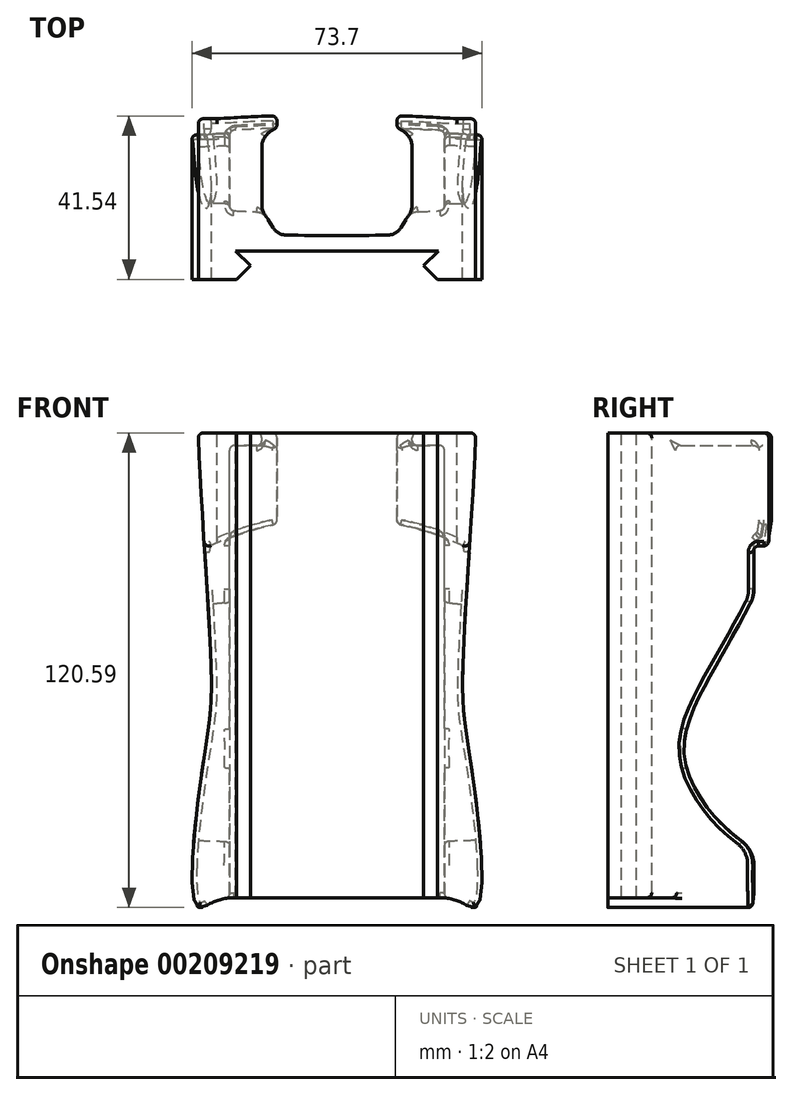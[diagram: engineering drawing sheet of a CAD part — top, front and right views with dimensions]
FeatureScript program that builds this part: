
annotation { "Feature Type Name" : "Feature", "Feature Type Description" : "" }
export const myFeature = defineFeature(function(context is Context, id is Id, definition is map)
    precondition{}
    {
        {
            var Q0;
            Q0=qCreatedBy(makeId("Top.planeOp"),FACE);
            var sketch = newSketch(context, id + "F0", { "sketchPlane" : qUnion([Q0])});
            skLineSegment(sketch, "E0", {"start": v(30.48, -10.36) * mm, "end": v(30.48, 30.47) * mm});
            skLineSegment(sketch, "E1", {"start": v(27.3, 27.49) * mm, "end": v(27.3, 7.17) * mm});
            skArc(sketch, "E2", {"start": v(20.63, 6.82) * mm, "mid": v(23.97, 6.98) * mm, "end": v(27.3, 7.17) * mm});
            skArc(sketch, "E3", {"start": v(0, 0.76) * mm, "mid": v(6.56, 0.8) * mm, "end": v(13.12, 0.95) * mm});
            skLineSegment(sketch, "E4", {"start": v(16.3, 2.85) * mm, "end": v(17.5, 4.91) * mm});
            skPoint(sketch, "E5.orphan", {"position": v(15.25, 1.01) * mm});
            skPoint(sketch, "E6.visualSharp", {"position": v(18.55, 6.73) * mm});
            skArc(sketch, "E6.filletArc", {"start": v(20.63, 6.82) * mm, "mid": v(18.82, 6.27) * mm, "end": v(17.5, 4.91) * mm});
            skArc(sketch, "E7.filletArc", {"start": v(13.12, 0.95) * mm, "mid": v(14.96, 1.48) * mm, "end": v(16.3, 2.85) * mm});
            skLineSegment(sketch, "E8", {"start": v(0, 0) * mm, "end": v(0, -3.13) * mm});
            skArc(sketch, "E9", {"start": v(27.3, 27.49) * mm, "mid": v(21.28, 27.8) * mm, "end": v(15.25, 28.05) * mm});
            skArc(sketch, "E10", {"start": v(30.48, 30.47) * mm, "mid": v(22.87, 30.9) * mm, "end": v(15.25, 31.22) * mm});
            skPoint(sketch, "E11.start.orphan", {"position": v(30.48, 27.99) * mm});
            skLineSegment(sketch, "E12.trimOffspring", {"start": v(0, 0.76) * mm, "end": v(0, -3.13) * mm});
            skLineSegment(sketch, "E13", {"start": v(15.25, 31.22) * mm, "end": v(15.25, 28.05) * mm});
            skLineSegment(sketch, "E14", {"start": v(0, -3.13) * mm, "end": v(25.78, -3.13) * mm});
            skLineSegment(sketch, "E15", {"start": v(25.78, -3.13) * mm, "end": v(22.02, -6.89) * mm});
            skLineSegment(sketch, "E16", {"start": v(0, -6.89) * mm, "end": v(29.89, -6.89) * mm, "construction": true});
            skLineSegment(sketch, "E17", {"start": v(25.5, -10.36) * mm, "end": v(30.48, -10.36) * mm});
            skLineSegment(sketch, "E18", {"start": v(22.02, -6.89) * mm, "end": v(25.5, -10.36) * mm});
            skSolve(sketch);
        }
        {
            var Q0;
            Q0=qSketchRegion(id+"F0",true);
            extrude(context, id + "F1", {"entities" : qUnion([Q0]), "oppositeDirection" : true, "depth" : 118.11 * mm});
        }
        {
            var Q0;
            Q0=makeQuery(id+"F1.opExtrude","SWEPT_FACE",FACE,{"disambiguationData":[OSD([sQuery(id+"F0.wireOp",EDGE,"E17")])]});
            var sketch = newSketch(context, id + "F2", { "sketchPlane" : qUnion([Q0])});
            skLineSegment(sketch, "E19", {"start": v(30.48, 0) * mm, "end": v(35.28, 0) * mm});
            skFitSpline(sketch, "E20", {"points": [v(30.48, -118.11) * mm, v(35.61, -120.17) * mm, v(33.76, -82.17) * mm, v(31.9, -64.6) * mm, v(33.93, -25.26) * mm, v(35.28, 0) * mm], "startDerivative": vector(61.38, -50.25) * mm, "endDerivative": vector(5.05, 107.66) * mm});
            skLineSegment(sketch, "E21", {"start": v(30.48, -118.11) * mm, "end": v(30.48, 0) * mm});
            skSolve(sketch);
        }
        {
            var Q0;
            Q0=qSketchRegion(id+"F2",true);
            var Q1;
            Q1=makeQuery(id+"F1.opExtrude","SWEPT_FACE",FACE,{"disambiguationData":[OSD([sQuery(id+"F0.wireOp",EDGE,"E10")])]});
            extrude(context, id + "F3", {"entities" : qUnion([Q0]), "operationType" : NewBodyOperationType.ADD, "oppositeDirection" : true, "endBoundEntityFace" : qUnion([Q1]), "depth" : 40.84 * mm});
        }
        {
            var Q0;
            Q0=makeQuery(id+"F1.opExtrude","CAP_VERTEX",VERTEX,{"disambiguationData":[OSD([sQuery(id+"F0.wireOp",EDGE,"E0"),sQuery(id+"F0.wireOp",EDGE,"E10")])],"isStart":false});
            var Q1;
            Q1=makeQuery(id+"F1.opExtrude","CAP_VERTEX",VERTEX,{"disambiguationData":[OSD([sQuery(id+"F0.wireOp",EDGE,"E0"),sQuery(id+"F0.wireOp",EDGE,"E10")])],"isStart":true});
            var Q2;
            Q2=makeQuery(id+"F1.opExtrude","CAP_VERTEX",VERTEX,{"disambiguationData":[OSD([sQuery(id+"F0.wireOp",EDGE,"E10"),sQuery(id+"F0.wireOp",EDGE,"MdokXZck-MeQf-Ru8W-Up0K-fHNruu8GMaJc")])],"isStart":true});
            cPlane(context, id + "F4", {"entities" : qUnion([Q0, Q1, Q2]), "cplaneType" : CPlaneType.THREE_POINT, "offset" : 50.8 * mm, "oppositeDirection" : true, "width" : 152.4 * mm, "height" : 152.4 * mm});
        }
        {
            var Q0;
            Q0=qCreatedBy(id+"F4.planeOp",FACE);
            var sketch = newSketch(context, id + "F5", { "sketchPlane" : qUnion([Q0])});
            skLineSegment(sketch, "E22", {"start": v(1.4, 0) * mm, "end": v(1.4, -106.44) * mm, "construction": true});
            skCircle(sketch, "E23", {"center": v(1.4, -97.8) * mm, "radius": 76.2 * mm});
            skSolve(sketch);
        }
        {
            var Q0;
            Q0=qSketchRegion(id+"F5",true);
            extrude(context, id + "F6", {"entities" : qUnion([Q0]), "operationType" : NewBodyOperationType.REMOVE, "oppositeDirection" : true, "depth" : 3.8 * mm, "hasSecondDirection" : true, "secondDirectionBound" : SecondDirectionBoundingType.THROUGH_ALL, "secondDirectionOppositeDirection" : false, "secondDirectionDepth" : 25.4 * mm});
        }
        {
            var Q0;
            Q0=qCreatedBy(makeId("Top.planeOp"),FACE);
            var sketch = newSketch(context, id + "F7", { "sketchPlane" : qUnion([Q0])});
            skLineSegment(sketch, "E24", {"start": v(19.1, 29.35) * mm, "end": v(27.88, 29.04) * mm});
            skLineSegment(sketch, "E25", {"start": v(27.88, 29.04) * mm, "end": v(27.88, 0) * mm});
            skLineSegment(sketch, "E26", {"start": v(27.88, 0) * mm, "end": v(19.1, 0) * mm});
            skLineSegment(sketch, "E27", {"start": v(19.1, 0) * mm, "end": v(19.1, 29.35) * mm});
            skPoint(sketch, "E28.orphan", {"position": v(0, 30.02) * mm});
            skSolve(sketch);
        }
        {
            var Q0;
            Q0=qSketchRegion(id+"F7",true);
            extrude(context, id + "F8", {"entities" : qUnion([Q0]), "operationType" : NewBodyOperationType.ADD, "oppositeDirection" : true, "depth" : 3.17 * mm});
        }
        {
            var Q0;
            Q0=makeQuery(id+"F1.opExtrude","SWEPT_FACE",FACE,{"disambiguationData":[OSD([sQuery(id+"F0.wireOp",EDGE,"E1")])]});
            var sketch = newSketch(context, id + "F9", { "sketchPlane" : qUnion([Q0])});
            skLineSegment(sketch, "E29", {"start": v(-29.4, -36.02) * mm, "end": v(-29.4, -107.37) * mm});
            skFitSpline(sketch, "E30", {"points": [v(-29.4, -36.02) * mm, v(-14.24, -64.34) * mm, v(-9.36, -84.1) * mm, v(-29.4, -107.37) * mm], "startDerivative": vector(39.36, -85.52) * mm, "endDerivative": vector(-85.37, -44.58) * mm});
            skSolve(sketch);
        }
        {
            var Q0;
            {var subQ0=sQuery(id+"F9.wireOp",EDGE,"E30");var subQ1=makeQuery(id+"F6.boolean.opBoolean","INTERSECT",EDGE,{"derivedFrom":[makeQuery(id+"F1.opExtrude","SWEPT_FACE",FACE,{"disambiguationData":[OSD([sQuery(id+"F0.wireOp",EDGE,"E1")])]}),makeQuery(id+"F6.opExtrude","CAP_FACE",FACE,{"disambiguationData":[OSD([sQuery(id+"F5.wireOp",EDGE,"E23")])],"isStart":false})]});var subQ2=makeQuery(id+"F9.imprint","INTERSECT",VERTEX,{"disambiguationData":[OD(0.0)],"derivedFrom":[subQ1,subQ0]});Q0=makeQuery(id+"F9.imprint","IMPRINT",FACE,{"disambiguationData":[TD([[makeQuery(id+"F9.imprint","IMPRINT",EDGE,{"disambiguationData":[TD([[subQ2,-1.0]])],"derivedFrom":subQ0}),-1.0]])]});}
            extrude(context, id + "F10", {"entities" : qUnion([Q0]), "operationType" : NewBodyOperationType.REMOVE, "endBound" : BoundingType.THROUGH_ALL, "oppositeDirection" : true, "depth" : 25.4 * mm});
        }
        {
            var Q0;
            Q0=makeQuery(id+"F10.boolean.opBoolean","INTERSECT",EDGE,{"disambiguationData":[OD(1.0)],"derivedFrom":[makeQuery(id+"F6.boolean.opBoolean","COPY",FACE,{"derivedFrom":makeQuery(id+"F6.opExtrude","CAP_FACE",FACE,{"disambiguationData":[OSD([sQuery(id+"F5.wireOp",EDGE,"E23")])],"isStart":false})}),makeQuery(id+"F10.opExtrude","SWEPT_FACE",FACE,{"disambiguationData":[OSD([sQuery(id+"F9.wireOp",EDGE,"E30")])]})]});
            var Q1;
            Q1=makeQuery(id+"F10.boolean.opBoolean","INTERSECT",EDGE,{"disambiguationData":[OD(0.0)],"derivedFrom":[makeQuery(id+"F6.boolean.opBoolean","COPY",FACE,{"derivedFrom":makeQuery(id+"F6.opExtrude","CAP_FACE",FACE,{"disambiguationData":[OSD([sQuery(id+"F5.wireOp",EDGE,"E23")])],"isStart":false})}),makeQuery(id+"F10.opExtrude","SWEPT_FACE",FACE,{"disambiguationData":[OSD([sQuery(id+"F9.wireOp",EDGE,"E30")])]})]});
            fillet(context, id + "F11", {"entities" : qUnion([Q0, Q1]), "radius" : 7.62 * mm, "tangentPropagation" : true, "allowEdgeOverflow" : false});
        }
        {
            var Q0;
            Q0=makeQuery(id+"F8.boolean.opBoolean","INTERSECT",EDGE,{"derivedFrom":[makeQuery(id+"F1.opExtrude","SWEPT_FACE",FACE,{"disambiguationData":[OSD([sQuery(id+"F0.wireOp",EDGE,"E9")])]}),makeQuery(id+"F8.opExtrude","SWEPT_FACE",FACE,{"disambiguationData":[OSD([sQuery(id+"F7.wireOp",EDGE,"E27")])]})]});
            fillet(context, id + "F12", {"entities" : qUnion([Q0]), "radius" : 5.08 * mm, "tangentPropagation" : true, "allowEdgeOverflow" : false});
        }
        {
            var Q0;
            Q0=makeQuery(id+"F8.boolean.opBoolean","INTERSECT",EDGE,{"derivedFrom":[makeQuery(id+"F1.opExtrude","SWEPT_FACE",FACE,{"disambiguationData":[OSD([sQuery(id+"F0.wireOp",EDGE,"E6.filletArc")])]}),makeQuery(id+"F8.opExtrude","SWEPT_FACE",FACE,{"disambiguationData":[OSD([sQuery(id+"F7.wireOp",EDGE,"E27")])]})]});
            fillet(context, id + "F13", {"entities" : qUnion([Q0]), "radius" : 5.08 * mm, "tangentPropagation" : true, "allowEdgeOverflow" : false});
        }
        {
            var Q0;
            Q0=makeQuery(id+"F3.boolean.opBoolean","MERGE",EDGE,{"derivedFrom":[makeQuery(id+"F1.opExtrude","CAP_EDGE",EDGE,{"disambiguationData":[OSD([sQuery(id+"F0.wireOp",EDGE,"E0")])],"isStart":false}),makeQuery(id+"F3.opExtrude","SWEPT_EDGE",EDGE,{"disambiguationData":[OSD([sQuery(id+"F0.wireOp",EDGE,"E17"),sQuery(id+"F2.wireOp",EDGE,"E20"),sQuery(id+"F2.wireOp",EDGE,"E21")])]})]});
            fillet(context, id + "F14", {"entities" : qUnion([Q0]), "radius" : 12.7 * mm, "tangentPropagation" : true, "allowEdgeOverflow" : false});
        }
        {
            var Q0;
            Q0=makeQuery(id+"F10.boolean.opBoolean","INTERSECT",EDGE,{"derivedFrom":[makeQuery(id+"F3.opExtrude","SWEPT_FACE",FACE,{"disambiguationData":[OSD([sQuery(id+"F2.wireOp",EDGE,"E20")])]}),makeQuery(id+"F10.opExtrude","SWEPT_FACE",FACE,{"disambiguationData":[OSD([sQuery(id+"F9.wireOp",EDGE,"E30")])]})]});
            var Q1;
            Q1=makeQuery(id+"F10.boolean.opBoolean","COPY",EDGE,{"derivedFrom":makeQuery(id+"F10.opExtrude","CAP_EDGE",EDGE,{"disambiguationData":[OSD([sQuery(id+"F9.wireOp",EDGE,"E30")])],"isStart":true})});
            fillet(context, id + "F15", {"entities" : qUnion([Q0, Q1]), "radius" : 1.27 * mm, "tangentPropagation" : true, "allowEdgeOverflow" : false});
        }
        {
            var Q0;
            Q0=makeQuery(id+"F6.boolean.opBoolean","INTERSECT",EDGE,{"derivedFrom":[makeQuery(id+"F1.opExtrude","SWEPT_FACE",FACE,{"disambiguationData":[OSD([sQuery(id+"F0.wireOp",EDGE,"E10")])]}),makeQuery(id+"F6.opExtrude","SWEPT_FACE",FACE,{"disambiguationData":[OSD([sQuery(id+"F5.wireOp",EDGE,"E23")])]})]});
            fillet(context, id + "F16", {"entities" : qUnion([Q0]), "radius" : 1.27 * mm, "tangentPropagation" : true, "allowEdgeOverflow" : false});
        }
        {
            var Q0;
            Q0=makeQuery(id+"F1.opExtrude","SWEPT_EDGE",EDGE,{"disambiguationData":[OSD([sQuery(id+"F0.wireOp",EDGE,"E1"),sQuery(id+"F0.wireOp",EDGE,"E2")])]});
            var Q1;
            Q1=makeQuery(id+"F8.boolean.opBoolean","INTERSECT",EDGE,{"derivedFrom":[makeQuery(id+"F1.opExtrude","SWEPT_FACE",FACE,{"disambiguationData":[OSD([sQuery(id+"F0.wireOp",EDGE,"E1")])]}),makeQuery(id+"F8.opExtrude","CAP_FACE",FACE,{"disambiguationData":[OSD([sQuery(id+"F7.wireOp",EDGE,"E24"),sQuery(id+"F7.wireOp",EDGE,"E25"),sQuery(id+"F7.wireOp",EDGE,"E26"),sQuery(id+"F7.wireOp",EDGE,"E27")])],"isStart":false})]});
            var Q2;
            Q2=makeQuery(id+"F1.opExtrude","SWEPT_EDGE",EDGE,{"disambiguationData":[OSD([sQuery(id+"F0.wireOp",EDGE,"E1"),sQuery(id+"F0.wireOp",EDGE,"E9")])]});
            var Q3;
            Q3=makeQuery(id+"F8.boolean.opBoolean","INTERSECT",EDGE,{"derivedFrom":[makeQuery(id+"F1.opExtrude","SWEPT_FACE",FACE,{"disambiguationData":[OSD([sQuery(id+"F0.wireOp",EDGE,"E9")])]}),makeQuery(id+"F8.opExtrude","CAP_FACE",FACE,{"disambiguationData":[OSD([sQuery(id+"F7.wireOp",EDGE,"E24"),sQuery(id+"F7.wireOp",EDGE,"E25"),sQuery(id+"F7.wireOp",EDGE,"E26"),sQuery(id+"F7.wireOp",EDGE,"E27")])],"isStart":false})]});
            fillet(context, id + "F17", {"entities" : qUnion([Q0, Q1, Q2, Q3]), "radius" : 1.27 * mm, "tangentPropagation" : true, "allowEdgeOverflow" : false});
        }
        {
            var Q0;
            Q0=makeQuery(id+"F6.boolean.opBoolean","INTERSECT",EDGE,{"derivedFrom":[makeQuery(id+"F1.opExtrude","SWEPT_FACE",FACE,{"disambiguationData":[OSD([sQuery(id+"F0.wireOp",EDGE,"E9")])]}),makeQuery(id+"F6.opExtrude","SWEPT_FACE",FACE,{"disambiguationData":[OSD([sQuery(id+"F5.wireOp",EDGE,"E23")])]})]});
            fillet(context, id + "F18", {"entities" : qUnion([Q0]), "radius" : 1.27 * mm, "tangentPropagation" : true, "allowEdgeOverflow" : false});
        }
        {
            var Q0;
            Q0=makeQuery(id+"F6.boolean.opBoolean","COPY",EDGE,{"derivedFrom":makeQuery(id+"F6.opExtrude","CAP_EDGE",EDGE,{"disambiguationData":[OSD([sQuery(id+"F5.wireOp",EDGE,"E23")])],"isStart":false})});
            fillet(context, id + "F19", {"entities" : qUnion([Q0]), "radius" : 1.27 * mm, "tangentPropagation" : true, "allowEdgeOverflow" : false});
        }
        {
            var Q0;
            Q0=makeQuery(id+"F6.boolean.opBoolean","INTERSECT",EDGE,{"derivedFrom":[makeQuery(id+"F3.opExtrude","CAP_FACE",FACE,{"disambiguationData":[OSD([sQuery(id+"F2.wireOp",EDGE,"E19"),sQuery(id+"F2.wireOp",EDGE,"E20"),sQuery(id+"F2.wireOp",EDGE,"E21")])],"isStart":false}),makeQuery(id+"F6.opExtrude","SWEPT_FACE",FACE,{"disambiguationData":[OSD([sQuery(id+"F5.wireOp",EDGE,"E23")])]})]});
            fillet(context, id + "F20", {"entities" : qUnion([Q0]), "radius" : 1.27 * mm, "tangentPropagation" : true, "allowEdgeOverflow" : false});
        }
        {
            var Q0;
            Q0=makeQuery(id+"F3.opExtrude","CAP_EDGE",EDGE,{"disambiguationData":[OSD([sQuery(id+"F2.wireOp",EDGE,"E20")])],"isStart":false});
            fillet(context, id + "F21", {"entities" : qUnion([Q0]), "radius" : 1.27 * mm, "tangentPropagation" : true, "allowEdgeOverflow" : false});
        }
        {
            var Q0;
            Q0=makeQuery(id+"F8.boolean.opBoolean","INTERSECT",EDGE,{"derivedFrom":[makeQuery(id+"F1.opExtrude","SWEPT_FACE",FACE,{"disambiguationData":[OSD([sQuery(id+"F0.wireOp",EDGE,"E2")])]}),makeQuery(id+"F8.opExtrude","CAP_FACE",FACE,{"disambiguationData":[OSD([sQuery(id+"F7.wireOp",EDGE,"E24"),sQuery(id+"F7.wireOp",EDGE,"E25"),sQuery(id+"F7.wireOp",EDGE,"E26"),sQuery(id+"F7.wireOp",EDGE,"E27")])],"isStart":false})]});
            var Q1;
            Q1=makeQuery(id+"F8.opExtrude","CAP_EDGE",EDGE,{"disambiguationData":[OSD([sQuery(id+"F7.wireOp",EDGE,"E27")])],"isStart":false});
            var Q2;
            Q2=makeQuery(id+"F8.opExtrude","CAP_EDGE",EDGE,{"disambiguationData":[OSD([sQuery(id+"F7.wireOp",EDGE,"E27")])],"isStart":true});
            var Q3;
            Q3=makeQuery(id+"F1.opExtrude","SWEPT_EDGE",EDGE,{"disambiguationData":[OSD([sQuery(id+"F0.wireOp",EDGE,"E9"),sQuery(id+"F0.wireOp",EDGE,"E13")])]});
            var Q4;
            Q4=makeQuery(id+"F1.opExtrude","CAP_EDGE",EDGE,{"disambiguationData":[OSD([sQuery(id+"F0.wireOp",EDGE,"E10")])],"isStart":true});
            var Q5;
            Q5=makeQuery(id+"F1.opExtrude","CAP_EDGE",EDGE,{"disambiguationData":[OSD([sQuery(id+"F0.wireOp",EDGE,"E13")])],"isStart":true});
            fillet(context, id + "F22", {"entities" : qUnion([Q0, Q1, Q2, Q3, Q4, Q5]), "radius" : 1.27 * mm, "tangentPropagation" : true, "allowEdgeOverflow" : false});
        }
        {
            var Q0;
            Q0=makeQuery(id+"F12.opFillet","BLEND_EDGE",EDGE,{"blendedFrom":[makeQuery(id+"F8.boolean.opBoolean","INTERSECT",EDGE,{"derivedFrom":[makeQuery(id+"F1.opExtrude","SWEPT_FACE",FACE,{"disambiguationData":[OSD([sQuery(id+"F0.wireOp",EDGE,"E9")])]}),makeQuery(id+"F8.opExtrude","SWEPT_FACE",FACE,{"disambiguationData":[OSD([sQuery(id+"F7.wireOp",EDGE,"E27")])]})]}),makeQuery(id+"F1.opExtrude","SWEPT_FACE",FACE,{"disambiguationData":[OSD([sQuery(id+"F0.wireOp",EDGE,"E13")])]})],"blendedInto":[makeQuery(id+"F1.opExtrude","SWEPT_FACE",FACE,{"disambiguationData":[OSD([sQuery(id+"F0.wireOp",EDGE,"E13")])]})]});
            fillet(context, id + "F23", {"entities" : qUnion([Q0]), "radius" : 1.27 * mm, "tangentPropagation" : true, "allowEdgeOverflow" : false});
        }
        {
            var Q0;
            Q0=makeQuery(id+"F3.opExtrude","SWEPT_EDGE",EDGE,{"disambiguationData":[OSD([sQuery(id+"F2.wireOp",EDGE,"E19"),sQuery(id+"F2.wireOp",EDGE,"E20")])]});
            fillet(context, id + "F24", {"entities" : qUnion([Q0]), "radius" : 1.27 * mm, "tangentPropagation" : true, "allowEdgeOverflow" : false});
        }
        {
            var Q0;
            Q0=makeQuery(id+"F1.opExtrude","CAP_EDGE",EDGE,{"disambiguationData":[OSD([sQuery(id+"F0.wireOp",EDGE,"E3")])],"isStart":false});
            fillet(context, id + "F25", {"entities" : qUnion([Q0]), "radius" : 1.27 * mm, "tangentPropagation" : true, "allowEdgeOverflow" : false});
        }
        {
            var Q0;
            Q0=makeQuery(id+"F1.opExtrude","SWEPT_BODY",BODY,{"disambiguationData":[OSD([sQuery(id+"F0.wireOp",EDGE,"2er3J34T-UetY-1yPx-DaCZ-OkgeTg1K8kIv"),sQuery(id+"F0.wireOp",EDGE,"E0"),sQuery(id+"F0.wireOp",EDGE,"E1"),sQuery(id+"F0.wireOp",EDGE,"E2"),sQuery(id+"F0.wireOp",EDGE,"E3"),sQuery(id+"F0.wireOp",EDGE,"E4"),sQuery(id+"F0.wireOp",EDGE,"E6.filletArc"),sQuery(id+"F0.wireOp",EDGE,"E7.filletArc"),sQuery(id+"F0.wireOp",EDGE,"tuMWJgsS-k7Jv-nQoi-J3SB-pvlRjHGqRAIn"),sQuery(id+"F0.wireOp",EDGE,"hivBriIb-3i2S-iEXT-tcMf-GkjieWFGtZ04"),sQuery(id+"F0.wireOp",EDGE,"E9"),sQuery(id+"F0.wireOp",EDGE,"E10"),sQuery(id+"F0.wireOp",EDGE,"E12.trimOffspring"),sQuery(id+"F0.wireOp",EDGE,"E13")])]});
            var Q1;
            Q1=qCreatedBy(makeId("Right.planeOp"),FACE);
            mirror(context, id + "F26", {"operationType" : NewBodyOperationType.ADD, "entities" : qUnion([Q0]), "mirrorPlane" : qUnion([Q1])});
        }
    });
